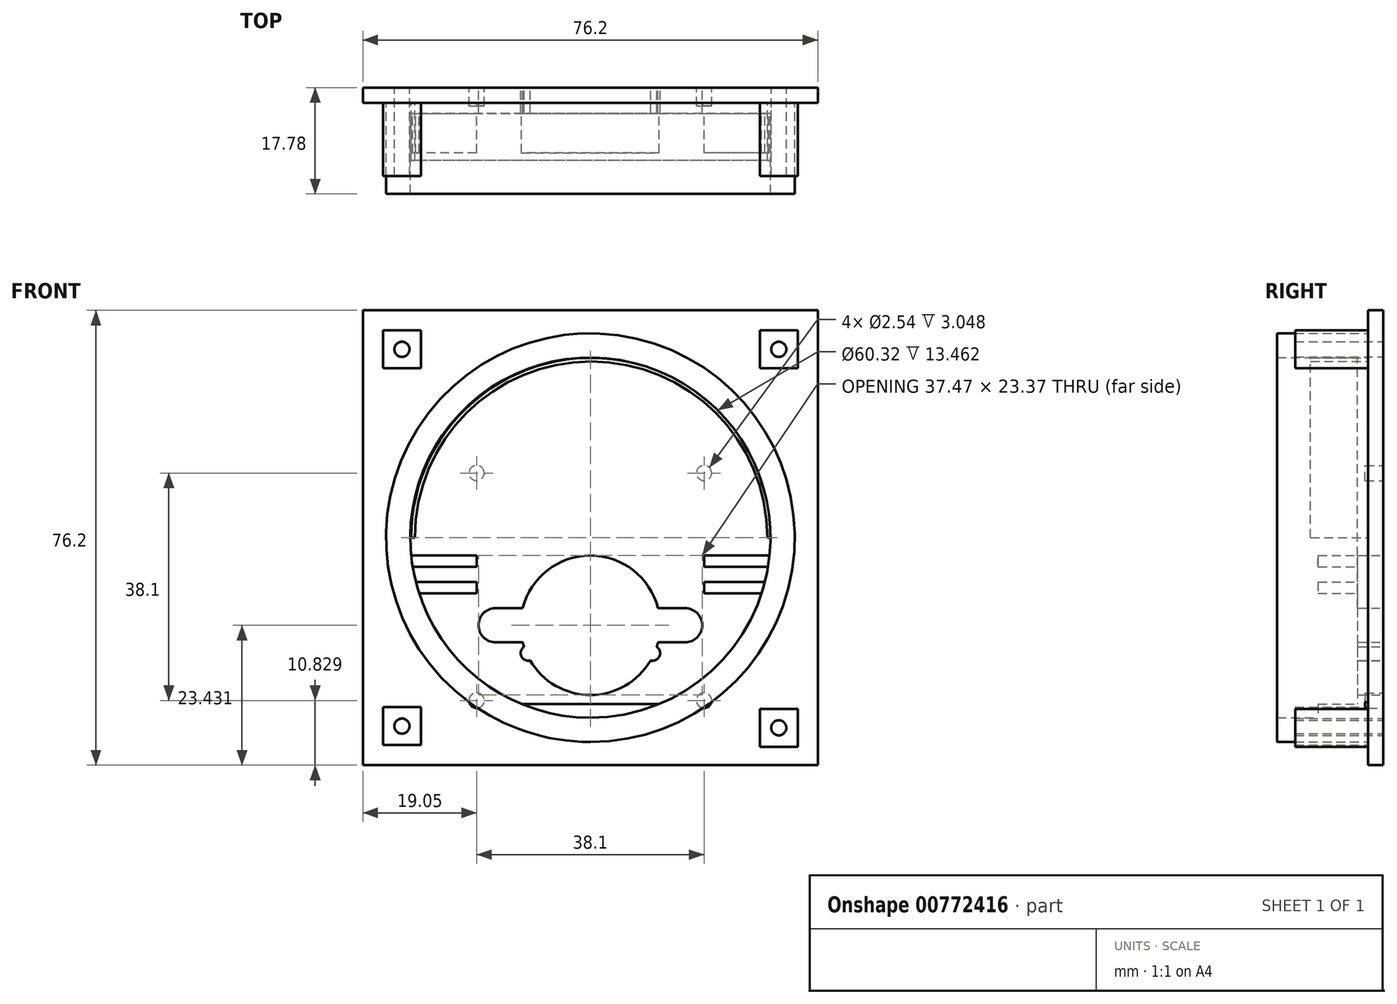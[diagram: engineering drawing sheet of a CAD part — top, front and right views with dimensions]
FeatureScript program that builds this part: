
annotation { "Feature Type Name" : "Feature", "Feature Type Description" : "" }
export const myFeature = defineFeature(function(context is Context, id is Id, definition is map)
    precondition{}
    {
        {
            var Q0;
            Q0=qCreatedBy(makeId("Front.planeOp"),FACE);
            var sketch = newSketch(context, id + "F0", { "sketchPlane" : qUnion([Q0])});
            skCircle(sketch, "E0", {"center": v(0, 0) * mm, "radius": 30.16 * mm});
            skCircle(sketch, "E1", {"center": v(0, -14.67) * mm, "radius": 11.68 * mm});
            skCircle(sketch, "E2", {"center": v(-15.88, -14.67) * mm, "radius": 2.86 * mm});
            skCircle(sketch, "E3", {"center": v(15.88, -14.67) * mm, "radius": 2.86 * mm});
            skPoint(sketch, "E4", {"position": v(-10.41, -19.34) * mm});
            skPoint(sketch, "E5", {"position": v(10.41, -19.34) * mm});
            skLineSegment(sketch, "E6.bottom", {"start": v(15.88, -11.81) * mm, "end": v(-15.88, -11.81) * mm});
            skLineSegment(sketch, "E6.top", {"start": v(15.88, -17.53) * mm, "end": v(-15.88, -17.53) * mm});
            skLineSegment(sketch, "E6.left", {"start": v(15.88, -11.81) * mm, "end": v(15.88, -17.53) * mm});
            skLineSegment(sketch, "E6.right", {"start": v(-15.88, -11.81) * mm, "end": v(-15.88, -17.53) * mm});
            skLineSegment(sketch, "E7.bottom", {"start": v(38.1, 38.1) * mm, "end": v(-38.1, 38.1) * mm});
            skLineSegment(sketch, "E7.top", {"start": v(38.1, -38.1) * mm, "end": v(-38.1, -38.1) * mm});
            skLineSegment(sketch, "E7.left", {"start": v(38.1, 38.1) * mm, "end": v(38.1, -38.1) * mm});
            skLineSegment(sketch, "E7.right", {"start": v(-38.1, 38.1) * mm, "end": v(-38.1, -38.1) * mm});
            skPoint(sketch, "E8", {"position": v(-31.56, 31.56) * mm});
            skPoint(sketch, "E9", {"position": v(31.56, 31.56) * mm});
            skPoint(sketch, "E10", {"position": v(31.56, -31.85) * mm});
            skPoint(sketch, "E11", {"position": v(-31.56, -31.56) * mm});
            skLineSegment(sketch, "E12.bottom", {"start": v(-28.38, 34.73) * mm, "end": v(-34.73, 34.73) * mm});
            skLineSegment(sketch, "E12.top", {"start": v(-28.38, 28.38) * mm, "end": v(-34.73, 28.38) * mm});
            skLineSegment(sketch, "E12.left", {"start": v(-28.38, 34.73) * mm, "end": v(-28.38, 28.38) * mm});
            skLineSegment(sketch, "E12.right", {"start": v(-34.73, 34.73) * mm, "end": v(-34.73, 28.38) * mm});
            skLineSegment(sketch, "E13.bottom", {"start": v(34.73, 34.73) * mm, "end": v(28.38, 34.73) * mm});
            skLineSegment(sketch, "E13.top", {"start": v(34.73, 28.38) * mm, "end": v(28.38, 28.38) * mm});
            skLineSegment(sketch, "E13.left", {"start": v(34.73, 34.73) * mm, "end": v(34.73, 28.38) * mm});
            skLineSegment(sketch, "E13.right", {"start": v(28.38, 34.73) * mm, "end": v(28.38, 28.38) * mm});
            skLineSegment(sketch, "E14.bottom", {"start": v(34.73, -28.68) * mm, "end": v(28.38, -28.68) * mm});
            skLineSegment(sketch, "E14.top", {"start": v(34.73, -35.03) * mm, "end": v(28.38, -35.03) * mm});
            skLineSegment(sketch, "E14.left", {"start": v(34.73, -28.68) * mm, "end": v(34.73, -35.03) * mm});
            skLineSegment(sketch, "E14.right", {"start": v(28.38, -28.68) * mm, "end": v(28.38, -35.03) * mm});
            skLineSegment(sketch, "E15.bottom", {"start": v(-28.38, -28.38) * mm, "end": v(-34.73, -28.38) * mm});
            skLineSegment(sketch, "E15.top", {"start": v(-28.38, -34.73) * mm, "end": v(-34.73, -34.73) * mm});
            skLineSegment(sketch, "E15.left", {"start": v(-28.38, -28.38) * mm, "end": v(-28.38, -34.73) * mm});
            skLineSegment(sketch, "E15.right", {"start": v(-34.73, -28.38) * mm, "end": v(-34.73, -34.73) * mm});
            skSolve(sketch);
        }
        {
            var Q0;
            Q0=makeQuery(id+"F0.imprint","IMPRINT",FACE,{"disambiguationData":[TD([[makeQuery(id+"F0.imprint","IMPRINT",EDGE,{"derivedFrom":sQuery(id+"F0.wireOp",EDGE,"E0")}),1.0]])]});
            extrude(context, id + "F1", {"entities" : qUnion([Q0]), "depth" : 4.32 * mm, "offsetDistance" : 25.4 * mm});
        }
        {
            var Q0;
            Q0=sQuery(id+"F0.wireOp",VERTEX,"E4");
            var Q1;
            Q1=sQuery(id+"F0.wireOp",VERTEX,"E5");
            var Q2;
            Q2=makeQuery(id+"F1.opExtrude","SWEPT_BODY",BODY,{"disambiguationData":[OSD([sQuery(id+"F0.wireOp",EDGE,"E0"),sQuery(id+"F0.wireOp",EDGE,"E1"),sQuery(id+"F0.wireOp",EDGE,"E2"),sQuery(id+"F0.wireOp",EDGE,"E3"),sQuery(id+"F0.wireOp",EDGE,"AQVEhfqM-bFfV-HZmN-Bbqf-DNwuXJOXuMRX.top"),sQuery(id+"F0.wireOp",EDGE,"FJdyEDiO-yEiY-Ot4F-tMeN-V1f38BCFD4gc.top")])]});
            hole(context, id + "F2", {"style" : HoleStyle.SIMPLE, "endStyle" : HoleEndStyle.THROUGH, "oppositeDirection" : true, "holeDiameter" : 2.54 * mm, "majorDiameter" : 6.35 * mm, "isTappedThrough" : true, "tappedDepth" : 12.7 * mm, "tapClearance" : 3, "locations" : qUnion([Q0, Q1]), "scope" : qUnion([Q2])});
        }
        {
            var Q0;
            {var subQ4=sQuery(id+"F0.wireOp",EDGE,"E6.right");Q0=makeQuery(id+"F0.imprint","IMPRINT",FACE,{"disambiguationData":[TD([[makeQuery(id+"F0.imprint","IMPRINT",EDGE,{"derivedFrom":subQ4}),1.0]])]});}
            var Q1;
            {var subQ0=sQuery(id+"F0.wireOp",EDGE,"E6.right");Q1=makeQuery(id+"F0.imprint","IMPRINT",FACE,{"disambiguationData":[TD([[makeQuery(id+"F0.imprint","IMPRINT",EDGE,{"derivedFrom":subQ0}),-1.0]])]});}
            var Q2;
            {var subQ4=sQuery(id+"F0.wireOp",EDGE,"E6.left");Q2=makeQuery(id+"F0.imprint","IMPRINT",FACE,{"disambiguationData":[TD([[makeQuery(id+"F0.imprint","IMPRINT",EDGE,{"derivedFrom":subQ4}),-1.0]])]});}
            var Q3;
            {var subQ0=sQuery(id+"F0.wireOp",EDGE,"E6.left");Q3=makeQuery(id+"F0.imprint","IMPRINT",FACE,{"disambiguationData":[TD([[makeQuery(id+"F0.imprint","IMPRINT",EDGE,{"derivedFrom":subQ0}),1.0]])]});}
            var Q4;
            {var subQ0=sQuery(id+"F0.wireOp",EDGE,"E6.bottom");var subQ1=sQuery(id+"F0.wireOp",EDGE,"E1");var subQ2=makeQuery(id+"F0.imprint","INTERSECT",VERTEX,{"disambiguationData":[OD(0.0)],"derivedFrom":[subQ1,subQ0]});Q4=makeQuery(id+"F0.imprint","IMPRINT",FACE,{"disambiguationData":[TD([[makeQuery(id+"F0.imprint","IMPRINT",EDGE,{"disambiguationData":[TD([[subQ2,-1.0]])],"derivedFrom":subQ1}),-1.0]])]});}
            var Q5;
            {var subQ0=sQuery(id+"F0.wireOp",EDGE,"E6.bottom");var subQ1=sQuery(id+"F0.wireOp",EDGE,"E1");var subQ2=makeQuery(id+"F0.imprint","INTERSECT",VERTEX,{"disambiguationData":[OD(1.0)],"derivedFrom":[subQ1,subQ0]});Q5=makeQuery(id+"F0.imprint","IMPRINT",FACE,{"disambiguationData":[TD([[makeQuery(id+"F0.imprint","IMPRINT",EDGE,{"disambiguationData":[TD([[subQ2,1.0]])],"derivedFrom":subQ1}),-1.0]])]});}
            extrude(context, id + "F3", {"entities" : qUnion([Q0, Q1, Q2, Q3, Q4, Q5]), "operationType" : NewBodyOperationType.REMOVE, "oppositeDirection" : true, "depth" : 10.92 * mm, "offsetDistance" : 25.4 * mm});
        }
        {
            var Q0;
            Q0=qCreatedBy(makeId("Front.planeOp"),FACE);
            var sketch = newSketch(context, id + "F4", { "sketchPlane" : qUnion([Q0])});
            skCircle(sketch, "E16", {"center": v(0, 0) * mm, "radius": 30.16 * mm});
            skCircle(sketch, "E17", {"center": v(0, 0) * mm, "radius": 34.23 * mm});
            skSolve(sketch);
        }
        {
            var Q0;
            Q0=qSketchRegion(id+"F4",true);
            extrude(context, id + "F5", {"entities" : qUnion([Q0]), "operationType" : NewBodyOperationType.ADD, "depth" : 17.78 * mm, "offsetDistance" : 25.4 * mm});
        }
        {
            var Q0;
            Q0=qCreatedBy(makeId("Front.planeOp"),FACE);
            cPlane(context, id + "F6", {"entities" : qUnion([Q0]), "cplaneType" : CPlaneType.OFFSET, "offset" : 2.54 * mm, "width" : 152.4 * mm, "height" : 152.4 * mm});
        }
        {
            var Q0;
            Q0=qCreatedBy(id+"F6.planeOp",FACE);
            var sketch = newSketch(context, id + "F7", { "sketchPlane" : qUnion([Q0])});
            skLineSegment(sketch, "E18.bottom", {"start": v(12.7, -27.88) * mm, "end": v(-12.7, -27.88) * mm});
            skLineSegment(sketch, "E18.top", {"start": v(12.7, -30.42) * mm, "end": v(-12.7, -30.42) * mm});
            skLineSegment(sketch, "E18.left", {"start": v(12.7, -27.88) * mm, "end": v(12.7, -30.42) * mm});
            skLineSegment(sketch, "E18.right", {"start": v(-12.7, -27.88) * mm, "end": v(-12.7, -30.42) * mm});
            skPoint(sketch, "E18.middle", {"position": v(0, -29.15) * mm});
            skLineSegment(sketch, "E19.bottom", {"start": v(-19.05, -2.98) * mm, "end": v(-31.75, -2.98) * mm});
            skLineSegment(sketch, "E19.top", {"start": v(-19.05, -9.33) * mm, "end": v(-31.75, -9.33) * mm});
            skLineSegment(sketch, "E19.left", {"start": v(-19.05, -2.98) * mm, "end": v(-19.05, -9.33) * mm});
            skLineSegment(sketch, "E19.right", {"start": v(-31.75, -2.98) * mm, "end": v(-31.75, -9.33) * mm});
            skPoint(sketch, "E19.middle", {"position": v(-25.4, -6.16) * mm});
            skLineSegment(sketch, "E20.bottom", {"start": v(31.75, -9.33) * mm, "end": v(19.05, -9.33) * mm});
            skLineSegment(sketch, "E20.top", {"start": v(31.75, -2.98) * mm, "end": v(19.05, -2.98) * mm});
            skLineSegment(sketch, "E20.left", {"start": v(31.75, -9.33) * mm, "end": v(31.75, -2.98) * mm});
            skLineSegment(sketch, "E20.right", {"start": v(19.05, -9.33) * mm, "end": v(19.05, -2.98) * mm});
            skPoint(sketch, "E20.middle", {"position": v(25.4, -6.16) * mm});
            skLineSegment(sketch, "E21.bottom", {"start": v(-19.05, -4.89) * mm, "end": v(-31.75, -4.89) * mm});
            skLineSegment(sketch, "E21.top", {"start": v(-19.05, -7.43) * mm, "end": v(-31.75, -7.43) * mm});
            skLineSegment(sketch, "E21.left", {"start": v(-19.05, -4.89) * mm, "end": v(-19.05, -7.43) * mm});
            skLineSegment(sketch, "E21.right", {"start": v(-31.75, -4.89) * mm, "end": v(-31.75, -7.43) * mm});
            skLineSegment(sketch, "E22.bottom", {"start": v(31.75, -4.89) * mm, "end": v(19.05, -4.89) * mm});
            skLineSegment(sketch, "E22.top", {"start": v(31.75, -7.43) * mm, "end": v(19.05, -7.43) * mm});
            skLineSegment(sketch, "E22.left", {"start": v(31.75, -4.89) * mm, "end": v(31.75, -7.43) * mm});
            skLineSegment(sketch, "E22.right", {"start": v(19.05, -4.89) * mm, "end": v(19.05, -7.43) * mm});
            skSolve(sketch);
        }
        {
            var Q0;
            Q0=makeQuery(id+"F0.imprint","IMPRINT",FACE,{"disambiguationData":[TD([[makeQuery(id+"F0.imprint","IMPRINT",EDGE,{"derivedFrom":sQuery(id+"F0.wireOp",EDGE,"E0")}),-1.0]])]});
            extrude(context, id + "F8", {"entities" : qUnion([Q0]), "operationType" : NewBodyOperationType.ADD, "depth" : 2.54 * mm, "offsetDistance" : 25.4 * mm});
        }
        {
            var Q0;
            Q0=qCreatedBy(id+"F6.planeOp",FACE);
            var sketch = newSketch(context, id + "F9", { "sketchPlane" : qUnion([Q0])});
            skArc(sketch, "E23", {"start": v(30.3, 0) * mm, "mid": v(0.13, 30.13) * mm, "end": v(-30.03, 0) * mm});
            skArc(sketch, "E24", {"start": v(29.66, 0) * mm, "mid": v(0.13, 29.53) * mm, "end": v(-29.4, 0) * mm});
            skLineSegment(sketch, "E25", {"start": v(-30.03, 0) * mm, "end": v(-29.4, 0) * mm});
            skLineSegment(sketch, "E26", {"start": v(29.66, 0) * mm, "end": v(30.3, 0) * mm});
            skSolve(sketch);
        }
        {
            var Q0;
            Q0=makeQuery(id+"F9.imprint","IMPRINT",FACE,{"disambiguationData":[TD([[makeQuery(id+"F9.imprint","IMPRINT",EDGE,{"derivedFrom":sQuery(id+"F9.wireOp",EDGE,"E23")}),1.0]])]});
            extrude(context, id + "F10", {"entities" : qUnion([Q0]), "depth" : 9.65 * mm, "offsetDistance" : 25.4 * mm});
        }
        {
            var Q0;
            Q0=qCreatedBy(makeId("Front.planeOp"),FACE);
            var sketch = newSketch(context, id + "F11", { "sketchPlane" : qUnion([Q0])});
            skCircle(sketch, "E27", {"center": v(19.05, 10.83) * mm, "radius": 1.27 * mm});
            skCircle(sketch, "E28", {"center": v(-19.05, 10.83) * mm, "radius": 1.27 * mm});
            skCircle(sketch, "E29", {"center": v(-19.05, -27.27) * mm, "radius": 1.27 * mm});
            skCircle(sketch, "E30", {"center": v(19.05, -27.27) * mm, "radius": 1.27 * mm});
            skSolve(sketch);
        }
        {
            var Q0;
            Q0=makeQuery(id+"F11.imprint","IMPRINT",FACE,{"disambiguationData":[TD([[makeQuery(id+"F11.imprint","IMPRINT",EDGE,{"derivedFrom":sQuery(id+"F11.wireOp",EDGE,"E27")}),1.0]])]});
            var Q1;
            Q1=makeQuery(id+"F11.imprint","IMPRINT",FACE,{"disambiguationData":[TD([[makeQuery(id+"F11.imprint","IMPRINT",EDGE,{"derivedFrom":sQuery(id+"F11.wireOp",EDGE,"E28")}),1.0]])]});
            var Q2;
            Q2=makeQuery(id+"F11.imprint","IMPRINT",FACE,{"disambiguationData":[TD([[makeQuery(id+"F11.imprint","IMPRINT",EDGE,{"derivedFrom":sQuery(id+"F11.wireOp",EDGE,"E29")}),1.0]])]});
            var Q3;
            Q3=makeQuery(id+"F11.imprint","IMPRINT",FACE,{"disambiguationData":[TD([[makeQuery(id+"F11.imprint","IMPRINT",EDGE,{"derivedFrom":sQuery(id+"F11.wireOp",EDGE,"E30")}),1.0]])]});
            extrude(context, id + "F12", {"entities" : qUnion([Q0, Q1, Q2, Q3]), "operationType" : NewBodyOperationType.REMOVE, "depth" : 3.05 * mm, "offsetDistance" : 25.4 * mm});
        }
        {
            var Q0;
            Q0=makeQuery(id+"F7.imprint","IMPRINT",FACE,{"disambiguationData":[TD([[makeQuery(id+"F7.imprint","IMPRINT",EDGE,{"derivedFrom":sQuery(id+"F7.wireOp",EDGE,"E18.bottom")}),1.0]])]});
            var Q1;
            {var subQ0=sQuery(id+"F7.wireOp",EDGE,"E19.bottom");Q1=makeQuery(id+"F7.imprint","IMPRINT",FACE,{"disambiguationData":[TD([[makeQuery(id+"F7.imprint","IMPRINT",EDGE,{"derivedFrom":subQ0}),1.0]])]});}
            var Q2;
            {var subQ0=sQuery(id+"F7.wireOp",EDGE,"E19.top");Q2=makeQuery(id+"F7.imprint","IMPRINT",FACE,{"disambiguationData":[TD([[makeQuery(id+"F7.imprint","IMPRINT",EDGE,{"derivedFrom":subQ0}),-1.0]])]});}
            var Q3;
            {var subQ0=sQuery(id+"F7.wireOp",EDGE,"E20.bottom");Q3=makeQuery(id+"F7.imprint","IMPRINT",FACE,{"disambiguationData":[TD([[makeQuery(id+"F7.imprint","IMPRINT",EDGE,{"derivedFrom":subQ0}),-1.0]])]});}
            var Q4;
            {var subQ0=sQuery(id+"F7.wireOp",EDGE,"E20.top");Q4=makeQuery(id+"F7.imprint","IMPRINT",FACE,{"disambiguationData":[TD([[makeQuery(id+"F7.imprint","IMPRINT",EDGE,{"derivedFrom":subQ0}),1.0]])]});}
            extrude(context, id + "F13", {"entities" : qUnion([Q0, Q1, Q2, Q3, Q4]), "operationType" : NewBodyOperationType.ADD, "depth" : 8.38 * mm, "offsetDistance" : 25.4 * mm});
        }
        {
            var Q0;
            Q0=makeQuery(id+"F0.imprint","IMPRINT",FACE,{"disambiguationData":[TD([[makeQuery(id+"F0.imprint","IMPRINT",EDGE,{"derivedFrom":sQuery(id+"F0.wireOp",EDGE,"E15.bottom")}),1.0]])]});
            var Q1;
            Q1=makeQuery(id+"F0.imprint","IMPRINT",FACE,{"disambiguationData":[TD([[makeQuery(id+"F0.imprint","IMPRINT",EDGE,{"derivedFrom":sQuery(id+"F0.wireOp",EDGE,"E12.bottom")}),1.0]])]});
            var Q2;
            Q2=makeQuery(id+"F0.imprint","IMPRINT",FACE,{"disambiguationData":[TD([[makeQuery(id+"F0.imprint","IMPRINT",EDGE,{"derivedFrom":sQuery(id+"F0.wireOp",EDGE,"E13.bottom")}),1.0]])]});
            var Q3;
            Q3=makeQuery(id+"F0.imprint","IMPRINT",FACE,{"disambiguationData":[TD([[makeQuery(id+"F0.imprint","IMPRINT",EDGE,{"derivedFrom":sQuery(id+"F0.wireOp",EDGE,"E14.bottom")}),1.0]])]});
            extrude(context, id + "F14", {"entities" : qUnion([Q0, Q1, Q2, Q3]), "operationType" : NewBodyOperationType.ADD, "depth" : 14.78 * mm, "offsetDistance" : 25.4 * mm});
        }
        {
            var Q0;
            Q0=sQuery(id+"F0.wireOp",VERTEX,"E8");
            var Q1;
            Q1=sQuery(id+"F0.wireOp",VERTEX,"E9");
            var Q2;
            Q2=sQuery(id+"F0.wireOp",VERTEX,"E11");
            var Q3;
            Q3=sQuery(id+"F0.wireOp",VERTEX,"E10");
            var Q4;
            Q4=makeQuery(id+"F1.opExtrude","SWEPT_BODY",BODY,{"disambiguationData":[OSD([sQuery(id+"F0.wireOp",EDGE,"E0"),sQuery(id+"F0.wireOp",EDGE,"E1"),sQuery(id+"F0.wireOp",EDGE,"E2"),sQuery(id+"F0.wireOp",EDGE,"E3"),sQuery(id+"F0.wireOp",EDGE,"E6.bottom"),sQuery(id+"F0.wireOp",EDGE,"E6.top")])]});
            hole(context, id + "F15", {"style" : HoleStyle.SIMPLE, "endStyle" : HoleEndStyle.THROUGH, "oppositeDirection" : true, "holeDiameter" : 2.54 * mm, "majorDiameter" : 6.35 * mm, "isTappedThrough" : true, "tappedDepth" : 12.7 * mm, "tapClearance" : 3, "locations" : qUnion([Q0, Q1, Q2, Q3]), "scope" : qUnion([Q4])});
        }
    });
